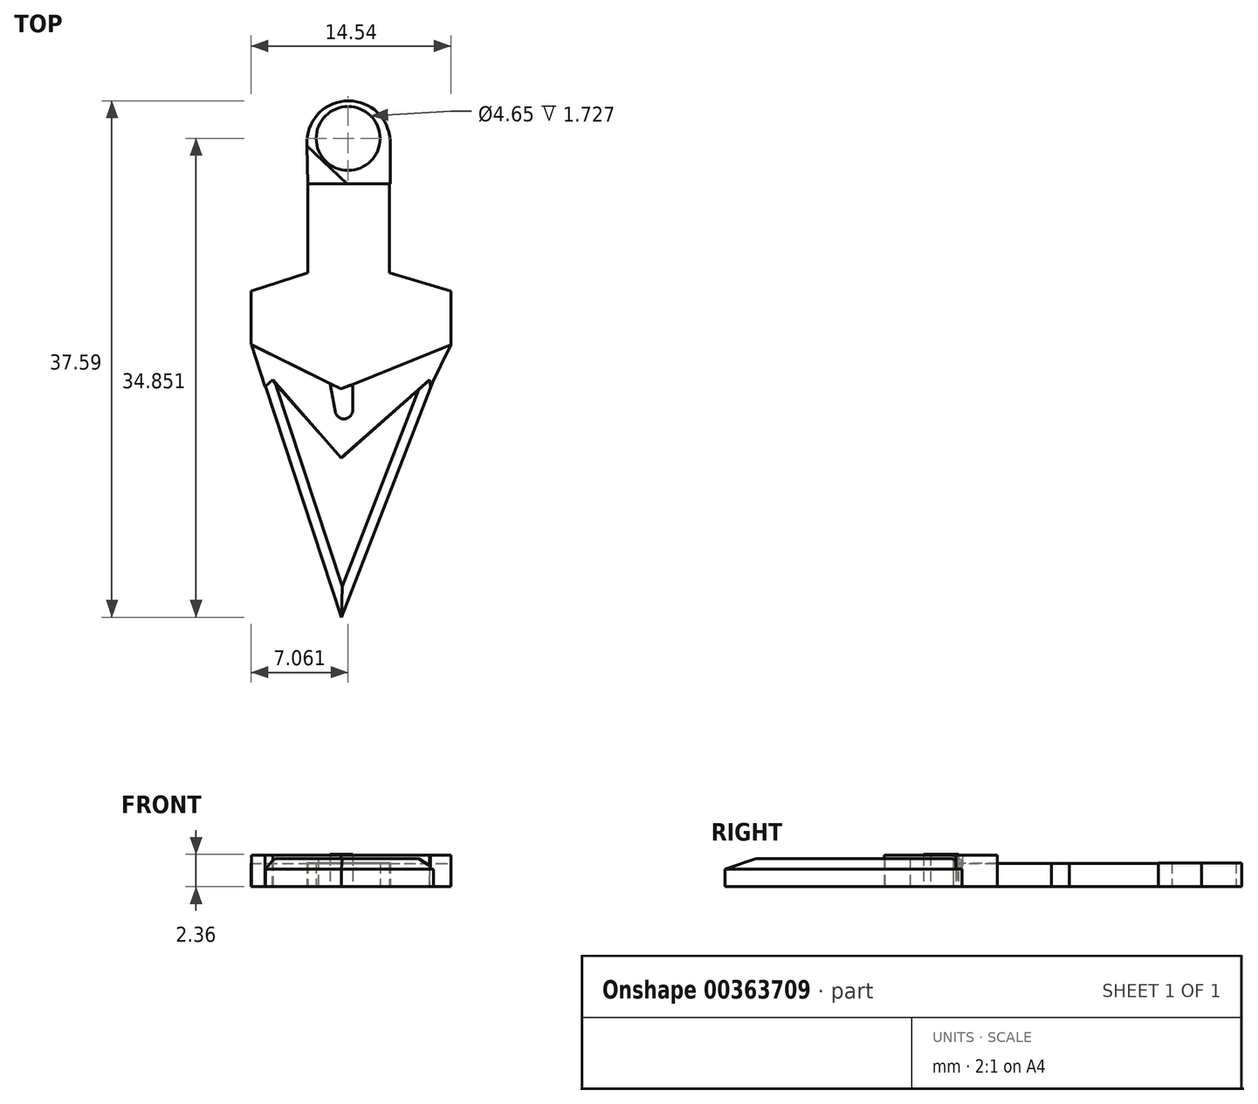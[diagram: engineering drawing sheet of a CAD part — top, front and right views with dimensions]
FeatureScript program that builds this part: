
annotation { "Feature Type Name" : "Feature", "Feature Type Description" : "" }
export const myFeature = defineFeature(function(context is Context, id is Id, definition is map)
    precondition{}
    {
        {
            var Q0;
            Q0=qCreatedBy(makeId("Top.planeOp"),FACE);
            var sketch = newSketch(context, id + "F0", { "sketchPlane" : qUnion([Q0])});
            skLineSegment(sketch, "E0", {"start": v(-76.08, -6.72) * mm, "end": v(-69.23, 10.94) * mm});
            skLineSegment(sketch, "E1", {"start": v(-69.23, 10.94) * mm, "end": v(-76.08, 4.87) * mm});
            skLineSegment(sketch, "E2", {"start": v(-76.08, 4.87) * mm, "end": v(-82.14, 11.7) * mm});
            skLineSegment(sketch, "E3", {"start": v(-82.14, 11.7) * mm, "end": v(-76.08, -6.72) * mm});
            skSolve(sketch);
        }
        {
            var Q0;
            Q0 = qSketchRegion(id + "F0", true);
            extrude(context, id + "F1", {"entities" : qUnion([Q0]), "depth" : 2.03 * mm});
        }
        {
            var Q0;
            Q0=makeQuery(id+"F1.opExtrude","CAP_EDGE",EDGE,{"disambiguationData":[OSD([sQuery(id+"F0.wireOp",EDGE,"E3")])],"isStart":false});
            var Q1;
            Q1=makeQuery(id+"F1.opExtrude","CAP_EDGE",EDGE,{"disambiguationData":[OSD([sQuery(id+"F0.wireOp",EDGE,"E0")])],"isStart":false});
            chamfer(context, id + "F2", {"entities" : qUnion([Q0, Q1]), "chamferType" : ChamferType.OFFSET_ANGLE, "width" : 0.76 * mm, "oppositeDirection" : false, "angle" : 45 * degree, "tangentPropagation" : true});
        }
        {
            var Q0;
            Q0=makeQuery(id+"F1.opExtrude","SWEPT_BODY",BODY,{"disambiguationData":[OSD([sQuery(id+"F0.wireOp",EDGE,"E0"),sQuery(id+"F0.wireOp",EDGE,"E1"),sQuery(id+"F0.wireOp",EDGE,"E2"),sQuery(id+"F0.wireOp",EDGE,"E3")])]});
            var Q1;
            Q1=qCreatedBy(makeId("Right.planeOp"),FACE);
            transform(context, id + "F3", {"entities" : qUnion([Q0]), "transformType" : TransformType.TRANSLATION_DISTANCE, "transformDirection" : qUnion([Q1]), "distance" : 62.74 * mm, "makeCopy" : false});
        }
        {
            var Q0;
            Q0=qCreatedBy(makeId("Top.planeOp"),FACE);
            var sketch = newSketch(context, id + "F4", { "sketchPlane" : qUnion([Q0])});
            skLineSegment(sketch, "E4", {"start": v(-13.39, 4.88) * mm, "end": v(-18.34, 10.57) * mm});
            skLineSegment(sketch, "E5", {"start": v(-18.34, 10.57) * mm, "end": v(-18.9, 10.08) * mm});
            skLineSegment(sketch, "E6", {"start": v(-18.9, 10.08) * mm, "end": v(-19.9, 13.1) * mm});
            skLineSegment(sketch, "E7", {"start": v(-19.9, 13.1) * mm, "end": v(-13.39, 9.9) * mm});
            skLineSegment(sketch, "E8", {"start": v(-6.92, 10.57) * mm, "end": v(-6.87, 10.08) * mm});
            skLineSegment(sketch, "E9", {"start": v(-6.87, 10.08) * mm, "end": v(-5.38, 13.1) * mm});
            skLineSegment(sketch, "E10", {"start": v(-5.38, 13.1) * mm, "end": v(-13.39, 9.9) * mm});
            skLineSegment(sketch, "E11", {"start": v(-14.17, 10.28) * mm, "end": v(-13.8, 8.24) * mm});
            skLineSegment(sketch, "E12", {"start": v(-12.54, 8.24) * mm, "end": v(-12.54, 10.28) * mm});
            skArc(sketch, "E13", {"start": v(-13.8, 8.24) * mm, "mid": v(-13.17, 7.72) * mm, "end": v(-12.54, 8.24) * mm});
            skLineSegment(sketch, "E14", {"start": v(-13.39, 4.88) * mm, "end": v(-6.92, 10.57) * mm});
            skSolve(sketch);
        }
        {
            var Q0;
            Q0 = qSketchRegion(id + "F4", true);
            extrude(context, id + "F5", {"entities" : qUnion([Q0]), "operationType" : NewBodyOperationType.ADD, "depth" : 2.3 * mm});
        }
        {
            var Q0;
            {var subQ6=sQuery(id+"F4.wireOp",EDGE,"E11");Q0=makeQuery(id+"F4.imprint","IMPRINT",FACE,{"disambiguationData":[TD([[makeQuery(id+"F4.imprint","IMPRINT",EDGE,{"derivedFrom":subQ6}),1.0]])]});}
            var Q1;
            Q1=sQuery(id+"F4.wireOp",EDGE,"E11");
            var Q2;
            Q2=sQuery(id+"F4.wireOp",EDGE,"E13");
            var Q3;
            Q3=sQuery(id+"F4.wireOp",EDGE,"E12");
            var Q4;
            Q4=sQuery(id+"F4.wireOp",EDGE,"E10");
            var Q5;
            Q5=sQuery(id+"F4.wireOp",EDGE,"E7");
            extrude(context, id + "F6", {"entities" : qUnion([Q0]), "surfaceEntities" : qUnion([Q1, Q2, Q3, Q4, Q5]), "depth" : 2.36 * mm});
        }
        {
            var Q0;
            Q0=qCreatedBy(makeId("Top.planeOp"),FACE);
            var sketch = newSketch(context, id + "F7", { "sketchPlane" : qUnion([Q0])});
            skLineSegment(sketch, "E15.MirrorCS", {"start": v(-5.38, 13.1) * mm, "end": v(-5.38, 17.03) * mm});
            skLineSegment(sketch, "E16", {"start": v(-19.92, 13.13) * mm, "end": v(-13.4, 9.9) * mm});
            skLineSegment(sketch, "E17", {"start": v(-13.4, 9.9) * mm, "end": v(-5.38, 13.1) * mm});
            skLineSegment(sketch, "E18", {"start": v(-19.92, 13.13) * mm, "end": v(-19.92, 17.03) * mm});
            skLineSegment(sketch, "E19", {"start": v(-19.92, 17.03) * mm, "end": v(-15.79, 18.35) * mm});
            skLineSegment(sketch, "E20", {"start": v(-15.79, 18.35) * mm, "end": v(-15.79, 24.82) * mm});
            skLineSegment(sketch, "E21", {"start": v(-15.79, 24.82) * mm, "end": v(-9.84, 24.82) * mm});
            skLineSegment(sketch, "E22", {"start": v(-9.84, 24.82) * mm, "end": v(-9.84, 18.35) * mm});
            skLineSegment(sketch, "E23", {"start": v(-9.84, 18.35) * mm, "end": v(-5.38, 17.03) * mm});
            skSolve(sketch);
        }
        {
            var Q0;
            Q0 = qSketchRegion(id + "F7", true);
            extrude(context, id + "F8", {"entities" : qUnion([Q0]), "depth" : 1.7 * mm});
        }
        {
            var Q0;
            Q0=qCreatedBy(makeId("Top.planeOp"),FACE);
            var sketch = newSketch(context, id + "F9", { "sketchPlane" : qUnion([Q0])});
            skCircle(sketch, "E24", {"center": v(-12.83, 27.85) * mm, "radius": 3.02 * mm});
            skLineSegment(sketch, "E25", {"start": v(-15.79, 24.82) * mm, "end": v(-12.9, 24.82) * mm, "construction": true});
            skLineSegment(sketch, "E26", {"start": v(-15.79, 24.82) * mm, "end": v(-15.85, 27.97) * mm});
            skLineSegment(sketch, "E27", {"start": v(-9.8, 27.97) * mm, "end": v(-9.8, 24.82) * mm});
            skPoint(sketch, "E27.endSnap0", {"position": v(-14.34, 24.82) * mm});
            skLineSegment(sketch, "E28", {"start": v(-9.8, 24.82) * mm, "end": v(-12.9, 24.82) * mm});
            skSolve(sketch);
        }
        {
            var Q0;
            {var subQ0=sQuery(id+"F9.wireOp",EDGE,"E26");var subQ1=sQuery(id+"F9.wireOp",EDGE,"E24");var subQ2=makeQuery(id+"F9.imprint","INTERSECT",VERTEX,{"disambiguationData":[OD(0.0)],"derivedFrom":[subQ1,subQ0]});Q0=makeQuery(id+"F9.imprint","IMPRINT",FACE,{"disambiguationData":[TD([[makeQuery(id+"F9.imprint","IMPRINT",EDGE,{"disambiguationData":[TD([[subQ2,1.0]])],"derivedFrom":subQ1}),1.0]])]});}
            var Q1;
            {var subQ0=sQuery(id+"F9.wireOp",EDGE,"E28");var subQ1=sQuery(id+"F9.wireOp",EDGE,"E24");var subQ2=makeQuery(id+"F9.imprint","INTERSECT",VERTEX,{"disambiguationData":[OD(1.0)],"derivedFrom":[subQ1,subQ0]});Q1=makeQuery(id+"F9.imprint","IMPRINT",FACE,{"disambiguationData":[TD([[makeQuery(id+"F9.imprint","IMPRINT",EDGE,{"disambiguationData":[TD([[subQ2,-1.0]])],"derivedFrom":subQ1}),-1.0]])]});}
            extrude(context, id + "F10", {"entities" : qUnion([Q0, Q1]), "operationType" : NewBodyOperationType.ADD, "depth" : 1.73 * mm});
        }
        {
            var Q0;
            Q0=qCreatedBy(makeId("Top.planeOp"),FACE);
            var sketch = newSketch(context, id + "F11", { "sketchPlane" : qUnion([Q0])});
            skCircle(sketch, "E29", {"center": v(-12.86, 28.13) * mm, "radius": 2.33 * mm});
            skSolve(sketch);
        }
        {
            var Q0;
            Q0 = qSketchRegion(id + "F11", true);
            extrude(context, id + "F12", {"entities" : qUnion([Q0]), "operationType" : NewBodyOperationType.REMOVE, "depth" : 6.6 * mm});
        }
        {
            var Q0;
            Q0=qCreatedBy(makeId("Top.planeOp"),FACE);
            var sketch = newSketch(context, id + "F13", { "sketchPlane" : qUnion([Q0])});
            skLineSegment(sketch, "E30", {"start": v(-15.84, 27.6) * mm, "end": v(-15.79, 24.82) * mm});
            skLineSegment(sketch, "E31", {"start": v(-15.79, 24.82) * mm, "end": v(-12.95, 24.82) * mm});
            skLineSegment(sketch, "E32", {"start": v(-12.95, 24.82) * mm, "end": v(-15.84, 27.6) * mm});
            skSolve(sketch);
        }
        {
            var Q0;
            Q0 = qSketchRegion(id + "F13", true);
            extrude(context, id + "F14", {"entities" : qUnion([Q0]), "operationType" : NewBodyOperationType.ADD, "depth" : 1.73 * mm});
        }
    });
